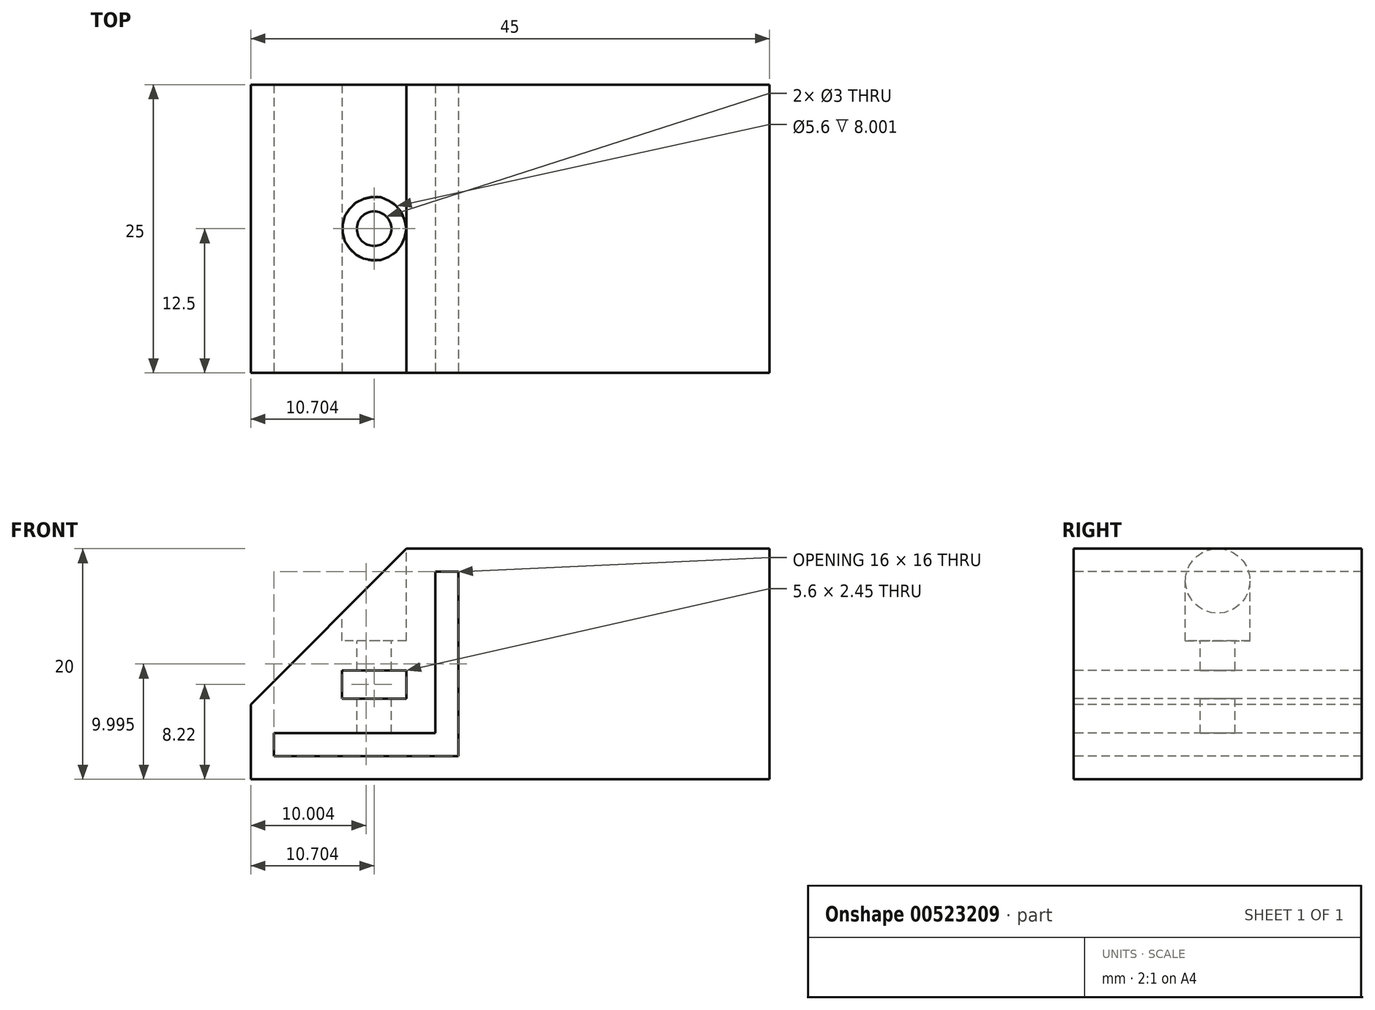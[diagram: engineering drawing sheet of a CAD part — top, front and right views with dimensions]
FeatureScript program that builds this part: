
annotation { "Feature Type Name" : "Feature", "Feature Type Description" : "" }
export const myFeature = defineFeature(function(context is Context, id is Id, definition is map)
    precondition{}
    {
        {
            var Q0;
            Q0=qCreatedBy(makeId("Front.planeOp"),FACE);
            var sketch = newSketch(context, id + "F0", { "sketchPlane" : qUnion([Q0])});
            skLineSegment(sketch, "E0.0", {"start": v(52.87, -38.21) * mm, "end": v(68.87, -38.21) * mm});
            skLineSegment(sketch, "E0.1", {"start": v(68.87, -22.21) * mm, "end": v(66.87, -22.21) * mm});
            skLineSegment(sketch, "E0.2", {"start": v(66.87, -22.21) * mm, "end": v(66.87, -36.21) * mm});
            skLineSegment(sketch, "E0.3", {"start": v(68.87, -38.21) * mm, "end": v(68.87, -22.21) * mm});
            skLineSegment(sketch, "E0.4", {"start": v(66.87, -36.21) * mm, "end": v(52.87, -36.21) * mm});
            skLineSegment(sketch, "E0.5", {"start": v(52.87, -36.21) * mm, "end": v(52.87, -38.21) * mm});
            skLineSegment(sketch, "E1", {"start": v(70.87, -40.21) * mm, "end": v(50.87, -40.21) * mm});
            skLineSegment(sketch, "E2", {"start": v(50.87, -40.21) * mm, "end": v(50.87, -33.71) * mm});
            skLineSegment(sketch, "E3", {"start": v(70.87, -40.21) * mm, "end": v(70.87, -20.21) * mm});
            skLineSegment(sketch, "E4", {"start": v(70.87, -20.21) * mm, "end": v(64.37, -20.21) * mm});
            skLineSegment(sketch, "E5", {"start": v(64.37, -20.21) * mm, "end": v(50.87, -33.71) * mm});
            skLineSegment(sketch, "E6.bottom", {"start": v(64.37, -33.21) * mm, "end": v(58.77, -33.21) * mm});
            skLineSegment(sketch, "E6.top", {"start": v(64.37, -30.76) * mm, "end": v(58.77, -30.76) * mm});
            skLineSegment(sketch, "E6.left", {"start": v(64.37, -33.21) * mm, "end": v(64.37, -30.76) * mm});
            skLineSegment(sketch, "E6.right", {"start": v(58.77, -33.21) * mm, "end": v(58.77, -30.76) * mm});
            skSolve(sketch);
        }
        {
            var Q0;
            Q0=makeQuery(id+"F0.imprint","IMPRINT",FACE,{"disambiguationData":[TD([[makeQuery(id+"F0.imprint","IMPRINT",EDGE,{"derivedFrom":sQuery(id+"F0.wireOp",EDGE,"E0.0")}),-1.0]])]});
            extrude(context, id + "F1", {"entities" : qUnion([Q0]), "oppositeDirection" : true, "depth" : 25 * mm, "offsetDistance" : 25 * mm});
        }
        {
            var Q0;
            Q0=makeQuery(id+"F1.opExtrude","SWEPT_FACE",FACE,{"disambiguationData":[OSD([sQuery(id+"F0.wireOp",EDGE,"E4")])]});
            var sketch = newSketch(context, id + "F2", { "sketchPlane" : qUnion([Q0])});
            skLineSegment(sketch, "E7.0.0", {"start": v(58.77, 0) * mm, "end": v(64.37, 0) * mm, "construction": true});
            skLineSegment(sketch, "E7.0.1", {"start": v(64.37, 0) * mm, "end": v(64.37, 25) * mm, "construction": true});
            skLineSegment(sketch, "E7.0.2", {"start": v(64.37, 25) * mm, "end": v(58.77, 25) * mm, "construction": true});
            skLineSegment(sketch, "E7.0.3", {"start": v(58.77, 25) * mm, "end": v(58.77, 0) * mm, "construction": true});
            skLineSegment(sketch, "E8", {"start": v(64.37, 0) * mm, "end": v(58.77, 25) * mm, "construction": true});
            skLineSegment(sketch, "E9", {"start": v(58.77, 0) * mm, "end": v(64.37, 25) * mm, "construction": true});
            skCircle(sketch, "E10", {"center": v(61.57, 12.5) * mm, "radius": 1.5 * mm});
            skSolve(sketch);
        }
        {
            var Q0;
            Q0=sQuery(id+"F2.wireOp",VERTEX,"E10.center");
            var Q1;
            Q1=makeQuery(id+"F1.opExtrude","SWEPT_BODY",BODY,{"disambiguationData":[OSD([sQuery(id+"F0.wireOp",EDGE,"E0.0"),sQuery(id+"F0.wireOp",EDGE,"E0.1"),sQuery(id+"F0.wireOp",EDGE,"E0.2"),sQuery(id+"F0.wireOp",EDGE,"E0.3"),sQuery(id+"F0.wireOp",EDGE,"E0.4"),sQuery(id+"F0.wireOp",EDGE,"E0.5"),sQuery(id+"F0.wireOp",EDGE,"E1"),sQuery(id+"F0.wireOp",EDGE,"E2"),sQuery(id+"F0.wireOp",EDGE,"E3"),sQuery(id+"F0.wireOp",EDGE,"E4"),sQuery(id+"F0.wireOp",EDGE,"E5"),sQuery(id+"F0.wireOp",EDGE,"E6.bottom"),sQuery(id+"F0.wireOp",EDGE,"E6.top"),sQuery(id+"F0.wireOp",EDGE,"E6.left"),sQuery(id+"F0.wireOp",EDGE,"E6.right")])]});
            hole(context, id + "F3", {"style" : HoleStyle.C_BORE, "endStyle" : HoleEndStyle.BLIND, "standardTappedOrClearance" : lookupTablePath({ "standard" : "ISO", "size" : "3", "type" : "Drilled" }), "standardBlindInLast" : lookupTablePath({ "standard" : "ISO", "size" : "3", "type" : "Drilled" }), "holeDiameter" : 3 * mm, "cBoreDiameter" : 5.6 * mm, "cBoreDepth" : 8 * mm, "holeDepth" : 16 * mm, "isTappedThrough" : true, "tappedDepth" : 12 * mm, "tapClearance" : 3, "startFromSketch" : true, "locations" : qUnion([Q0]), "scope" : qUnion([Q1])});
        }
        {
            var Q0;
            Q0=makeQuery(id+"F1.opExtrude","SWEPT_FACE",FACE,{"disambiguationData":[OSD([sQuery(id+"F0.wireOp",EDGE,"E3")])]});
            extrude(context, id + "F4", {"entities" : qUnion([Q0]), "operationType" : NewBodyOperationType.ADD, "depth" : 25 * mm, "offsetDistance" : 25 * mm});
        }
    });
